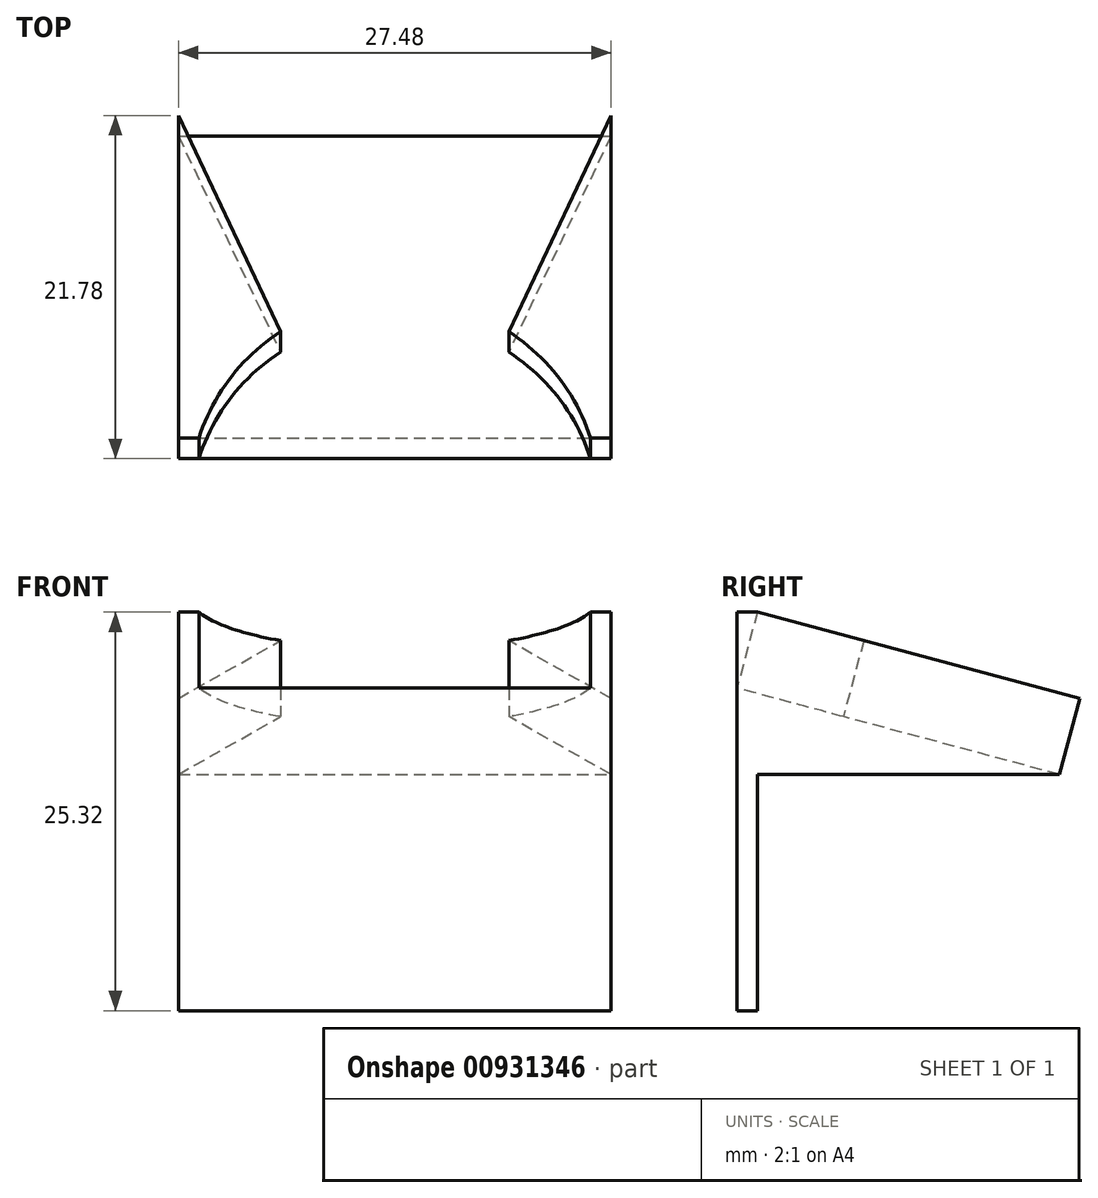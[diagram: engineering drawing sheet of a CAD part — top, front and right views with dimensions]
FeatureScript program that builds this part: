
annotation { "Feature Type Name" : "Feature", "Feature Type Description" : "" }
export const myFeature = defineFeature(function(context is Context, id is Id, definition is map)
    precondition{}
    {
        {
            var Q0;
            Q0=qCreatedBy(makeId("Top.planeOp"),FACE);
            var sketch = newSketch(context, id + "F0", { "sketchPlane" : qUnion([Q0])});
            skArc(sketch, "E0", {"start": v(-7.25, 7) * mm, "mid": v(-10.45, 3.95) * mm, "end": v(-12.44, 0) * mm});
            skLineSegment(sketch, "E1", {"start": v(-7.25, 7) * mm, "end": v(7.25, 7) * mm, "construction": true});
            skPoint(sketch, "E2", {"position": v(0, 7) * mm});
            skLineSegment(sketch, "E3", {"start": v(-12.5, 18.5) * mm, "end": v(12.5, 18.5) * mm, "construction": true});
            skPoint(sketch, "E4", {"position": v(0, 18.5) * mm});
            skLineSegment(sketch, "E5", {"start": v(-13.74, 21.2) * mm, "end": v(-7.25, 7) * mm});
            skLineSegment(sketch, "E6", {"start": v(13.74, 21.2) * mm, "end": v(7.25, 7) * mm});
            skLineSegment(sketch, "E7", {"start": v(13.74, 21.2) * mm, "end": v(13.74, 0) * mm});
            skLineSegment(sketch, "E8", {"start": v(-13.74, 21.2) * mm, "end": v(-13.74, 0) * mm});
            skArc(sketch, "E9.trimOffspring", {"start": v(12.44, 0) * mm, "mid": v(10.45, 3.95) * mm, "end": v(7.25, 7) * mm});
            skLineSegment(sketch, "E10", {"start": v(-13.74, 0) * mm, "end": v(-12.44, 0) * mm});
            skLineSegment(sketch, "E11.trimOffspring", {"start": v(12.44, 0) * mm, "end": v(13.74, 0) * mm});
            skLineSegment(sketch, "E12", {"start": v(-12.44, 0) * mm, "end": v(13.74, 0) * mm, "construction": true});
            skSolve(sketch);
        }
        {
            var Q0;
            Q0 = qSketchRegion(id + "F0", true);
            extrude(context, id + "F1", {"entities" : qUnion([Q0]), "surfaceOperationType" : NewSurfaceOperationType.ADD, "depth" : 5 * mm, "offsetDistance" : 25 * mm});
        }
        {
            var Q0;
            Q0=makeQuery(id+"F1.opExtrude","SWEPT_BODY",BODY,{"disambiguationData":[OSD([sQuery(id+"F0.wireOp",EDGE,"E0"),sQuery(id+"F0.wireOp",EDGE,"E5"),sQuery(id+"F0.wireOp",EDGE,"E8"),sQuery(id+"F0.wireOp",EDGE,"E10")])]});
            var Q1;
            Q1=makeQuery(id+"F1.opExtrude","SWEPT_BODY",BODY,{"disambiguationData":[OSD([sQuery(id+"F0.wireOp",EDGE,"E6"),sQuery(id+"F0.wireOp",EDGE,"E7"),sQuery(id+"F0.wireOp",EDGE,"E9.trimOffspring"),sQuery(id+"F0.wireOp",EDGE,"E11.trimOffspring")])]});
            var Q2;
            Q2=sQuery(id+"F0.wireOp",EDGE,"E12");
            transform(context, id + "F2", {"entities" : qUnion([Q0, Q1]), "transformType" : TransformType.ROTATION, "transformAxis" : qUnion([Q2]), "angle" : 15 * degree, "oppositeDirection" : true, "makeCopy" : false});
        }
        {
            var Q0;
            Q0=makeQuery(id+"F1.opExtrude","SWEPT_FACE",FACE,{"disambiguationData":[OSD([sQuery(id+"F0.wireOp",EDGE,"E7")])]});
            var sketch = newSketch(context, id + "F3", { "sketchPlane" : qUnion([Q0])});
            skLineSegment(sketch, "E13", {"start": v(0, 0) * mm, "end": v(0, -5.49) * mm});
            skLineSegment(sketch, "E14", {"start": v(20.48, -5.49) * mm, "end": v(0, -5.49) * mm});
            skLineSegment(sketch, "E15.0", {"start": v(20.48, -5.49) * mm, "end": v(0, 0) * mm});
            skSolve(sketch);
        }
        {
            var Q0;
            Q0 = qSketchRegion(id + "F3", true);
            var Q1;
            Q1=makeQuery(id+"F1.opExtrude","SWEPT_FACE",FACE,{"disambiguationData":[OSD([sQuery(id+"F0.wireOp",EDGE,"E8")])]});
            extrude(context, id + "F4", {"entities" : qUnion([Q0]), "operationType" : NewBodyOperationType.ADD, "endBound" : BoundingType.UP_TO_SURFACE, "oppositeDirection" : true, "depth" : 25 * mm, "endBoundEntityFace" : qUnion([Q1]), "offsetDistance" : 25 * mm});
        }
        {
            var Q0;
            Q0=makeQuery(id+"F4.opExtrude","SWEPT_FACE",FACE,{"disambiguationData":[OSD([sQuery(id+"F3.wireOp",EDGE,"E13")])]});
            var sketch = newSketch(context, id + "F5", { "sketchPlane" : qUnion([Q0])});
            skPoint(sketch, "E16.0", {"position": v(-13.74, -5.49) * mm});
            skPoint(sketch, "E17.0", {"position": v(13.74, -5.49) * mm});
            skLineSegment(sketch, "E18.bottom", {"start": v(-13.74, -5.49) * mm, "end": v(13.74, -5.49) * mm});
            skLineSegment(sketch, "E18.top", {"start": v(-13.74, -20.49) * mm, "end": v(13.74, -20.49) * mm});
            skLineSegment(sketch, "E18.left", {"start": v(-13.74, -5.49) * mm, "end": v(-13.74, -20.49) * mm});
            skLineSegment(sketch, "E18.right", {"start": v(13.74, -5.49) * mm, "end": v(13.74, -20.49) * mm});
            skSolve(sketch);
        }
        {
            var Q0;
            Q0 = qSketchRegion(id + "F5", true);
            extrude(context, id + "F6", {"entities" : qUnion([Q0]), "operationType" : NewBodyOperationType.ADD, "oppositeDirection" : true, "depth" : 1.3 * mm, "offsetDistance" : 25 * mm});
        }
        {
            var Q0;
            Q0=makeQuery(id+"F6.boolean.opBoolean","MERGE",FACE,{"derivedFrom":[makeQuery(id+"F4.opExtrude","SWEPT_FACE",FACE,{"disambiguationData":[OSD([sQuery(id+"F3.wireOp",EDGE,"E13")])]}),makeQuery(id+"F6.opExtrude","CAP_FACE",FACE,{"disambiguationData":[OSD([sQuery(id+"F5.wireOp",EDGE,"E18.bottom"),sQuery(id+"F5.wireOp",EDGE,"E18.top"),sQuery(id+"F5.wireOp",EDGE,"E18.left"),sQuery(id+"F5.wireOp",EDGE,"E18.right")])],"isStart":true})]});
            var sketch = newSketch(context, id + "F7", { "sketchPlane" : qUnion([Q0])});
            skPoint(sketch, "E19.0", {"position": v(-13.74, 0) * mm});
            skPoint(sketch, "E20.0", {"position": v(13.74, 4.83) * mm});
            skPoint(sketch, "E21.0", {"position": v(-12.44, 4.83) * mm});
            skPoint(sketch, "E22.0", {"position": v(12.44, 0) * mm});
            skLineSegment(sketch, "E23.bottom", {"start": v(-13.74, 0) * mm, "end": v(-12.44, 0) * mm});
            skLineSegment(sketch, "E23.top", {"start": v(-13.74, 4.83) * mm, "end": v(-12.44, 4.83) * mm});
            skLineSegment(sketch, "E23.left", {"start": v(-13.74, 0) * mm, "end": v(-13.74, 4.83) * mm});
            skLineSegment(sketch, "E23.right", {"start": v(-12.44, 0) * mm, "end": v(-12.44, 4.83) * mm});
            skLineSegment(sketch, "E24.bottom", {"start": v(12.44, 0) * mm, "end": v(13.74, 0) * mm});
            skLineSegment(sketch, "E24.top", {"start": v(12.44, 4.83) * mm, "end": v(13.74, 4.83) * mm});
            skLineSegment(sketch, "E24.left", {"start": v(12.44, 0) * mm, "end": v(12.44, 4.83) * mm});
            skLineSegment(sketch, "E24.right", {"start": v(13.74, 0) * mm, "end": v(13.74, 4.83) * mm});
            skSolve(sketch);
        }
        {
            var Q0;
            Q0 = qSketchRegion(id + "F7", true);
            var Q1;
            Q1=makeQuery(id+"F1.opExtrude","SWEPT_BODY",BODY,{"disambiguationData":[OSD([sQuery(id+"F0.wireOp",EDGE,"E0"),sQuery(id+"F0.wireOp",EDGE,"E5"),sQuery(id+"F0.wireOp",EDGE,"E8"),sQuery(id+"F0.wireOp",EDGE,"E10")])]});
            extrude(context, id + "F8", {"entities" : qUnion([Q0]), "operationType" : NewBodyOperationType.ADD, "endBound" : BoundingType.UP_TO_BODY, "oppositeDirection" : true, "depth" : 25 * mm, "endBoundEntityBody" : qUnion([Q1]), "offsetDistance" : 25 * mm});
        }
    });
